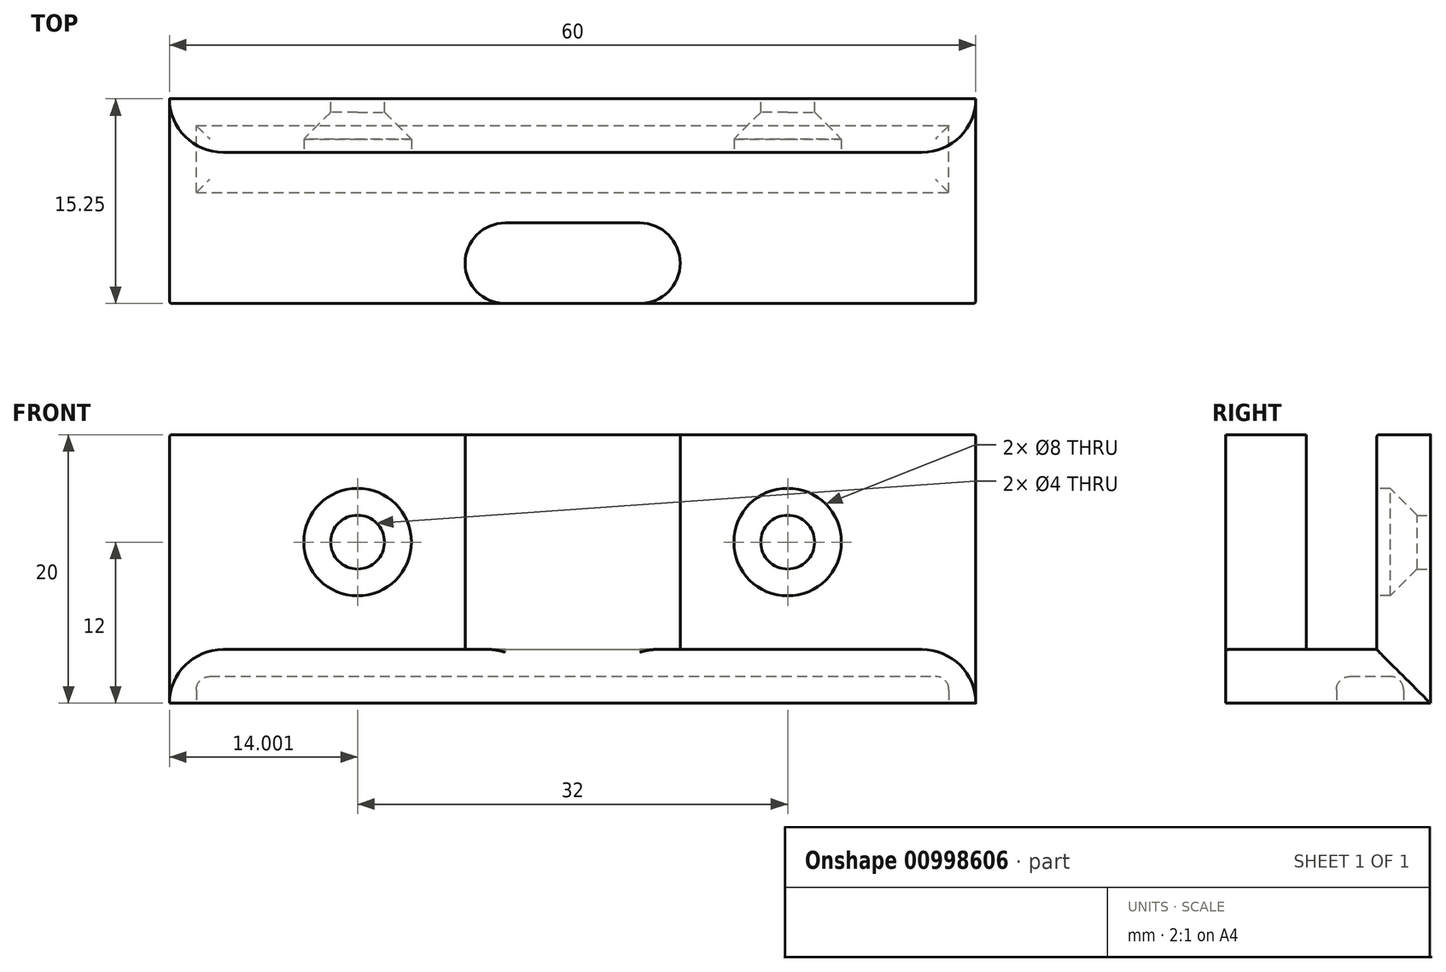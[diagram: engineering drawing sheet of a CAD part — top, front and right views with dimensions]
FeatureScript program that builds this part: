
annotation { "Feature Type Name" : "Feature", "Feature Type Description" : "" }
export const myFeature = defineFeature(function(context is Context, id is Id, definition is map)
    precondition{}
    {
        {
            var Q0;
            Q0=qCreatedBy(makeId("Top.planeOp"),FACE);
            var sketch = newSketch(context, id + "F0", { "sketchPlane" : qUnion([Q0])});
            skLineSegment(sketch, "E0.bottom", {"start": v(-19.65, 15.3) * mm, "end": v(40.35, 15.3) * mm});
            skLineSegment(sketch, "E0.top", {"start": v(-19.65, 0.05) * mm, "end": v(40.35, 0.05) * mm});
            skLineSegment(sketch, "E0.left", {"start": v(-19.65, 15.3) * mm, "end": v(-19.65, 0.05) * mm});
            skLineSegment(sketch, "E0.right", {"start": v(40.35, 15.3) * mm, "end": v(40.35, 0.05) * mm});
            skSolve(sketch);
        }
        {
            var Q0;
            Q0=makeQuery(id+"F0.imprint","IMPRINT",FACE,{"disambiguationData":[TD([[makeQuery(id+"F0.imprint","IMPRINT",EDGE,{"derivedFrom":sQuery(id+"F0.wireOp",EDGE,"E0.bottom")}),-1.0]])]});
            extrude(context, id + "F1", {"entities" : qUnion([Q0]), "depth" : 4 * mm, "offsetDistance" : 25 * mm});
        }
        {
            var Q0;
            Q0=makeQuery(id+"F1.opExtrude","CAP_FACE",FACE,{"disambiguationData":[OSD([sQuery(id+"F0.wireOp",EDGE,"E0.bottom"),sQuery(id+"F0.wireOp",EDGE,"E0.top"),sQuery(id+"F0.wireOp",EDGE,"E0.left"),sQuery(id+"F0.wireOp",EDGE,"E0.right")])],"isStart":false});
            var sketch = newSketch(context, id + "F2", { "sketchPlane" : qUnion([Q0])});
            skLineSegment(sketch, "E1.bottom", {"start": v(-19.65, 15.3) * mm, "end": v(40.35, 15.3) * mm});
            skLineSegment(sketch, "E1.top", {"start": v(-19.65, 11.3) * mm, "end": v(40.35, 11.3) * mm});
            skLineSegment(sketch, "E1.left", {"start": v(-19.65, 15.3) * mm, "end": v(-19.65, 11.3) * mm});
            skLineSegment(sketch, "E1.right", {"start": v(40.35, 15.3) * mm, "end": v(40.35, 11.3) * mm});
            skPoint(sketch, "E2", {"position": v(2.35, 3.05) * mm});
            skPoint(sketch, "E3", {"position": v(18.35, 3.05) * mm});
            skPoint(sketch, "E4", {"position": v(15.35, 6.05) * mm});
            skPoint(sketch, "E5", {"position": v(15.35, 0.05) * mm});
            skPoint(sketch, "E6", {"position": v(5.35, 6.05) * mm});
            skPoint(sketch, "E7", {"position": v(5.35, 0.05) * mm});
            skArc(sketch, "E8", {"start": v(5.35, 6.05) * mm, "mid": v(2.35, 3.05) * mm, "end": v(5.35, 0.05) * mm});
            skArc(sketch, "E9", {"start": v(15.35, 6.05) * mm, "mid": v(18.35, 3.05) * mm, "end": v(15.35, 0.05) * mm});
            skLineSegment(sketch, "E10", {"start": v(5.35, 6.05) * mm, "end": v(15.35, 6.05) * mm});
            skLineSegment(sketch, "E11", {"start": v(5.35, 0.05) * mm, "end": v(15.35, 0.05) * mm});
            skSolve(sketch);
        }
        {
            var Q0;
            Q0 = qSketchRegion(id + "F2", true);
            extrude(context, id + "F3", {"entities" : qUnion([Q0]), "operationType" : NewBodyOperationType.ADD, "depth" : 16 * mm, "offsetDistance" : 25 * mm});
        }
        {
            var Q0;
            Q0=makeQuery(id+"F3.opExtrude","SWEPT_FACE",FACE,{"disambiguationData":[OSD([sQuery(id+"F2.wireOp",EDGE,"E1.top")])]});
            var sketch = newSketch(context, id + "F4", { "sketchPlane" : qUnion([Q0])});
            skCircle(sketch, "E12", {"center": v(-5.65, 12) * mm, "radius": 4 * mm});
            skCircle(sketch, "E13", {"center": v(26.35, 12) * mm, "radius": 4 * mm});
            skSolve(sketch);
        }
        {
            var Q0;
            Q0 = qSketchRegion(id + "F4", true);
            extrude(context, id + "F5", {"entities" : qUnion([Q0]), "operationType" : NewBodyOperationType.REMOVE, "oppositeDirection" : true, "depth" : 1 * mm, "offsetDistance" : 25 * mm});
        }
        {
            var Q0;
            Q0=makeQuery(id+"F5.boolean.opBoolean","COPY",FACE,{"derivedFrom":makeQuery(id+"F5.opExtrude","CAP_FACE",FACE,{"disambiguationData":[OSD([sQuery(id+"F4.wireOp",EDGE,"E12")])],"isStart":false})});
            var Q1;
            Q1=makeQuery(id+"F5.boolean.opBoolean","COPY",FACE,{"derivedFrom":makeQuery(id+"F5.opExtrude","CAP_FACE",FACE,{"disambiguationData":[OSD([sQuery(id+"F4.wireOp",EDGE,"E13")])],"isStart":false})});
            extrude(context, id + "F6", {"entities" : qUnion([Q0, Q1]), "operationType" : NewBodyOperationType.REMOVE, "oppositeDirection" : true, "depth" : 25 * mm, "offsetDistance" : 25 * mm, "hasDraft" : true, "draftAngle" : 45 * degree, "draftPullDirection" : true});
        }
        {
            var Q0;
            Q0=makeQuery(id+"F3.boolean.opBoolean","MERGE",FACE,{"derivedFrom":[makeQuery(id+"F1.opExtrude","SWEPT_FACE",FACE,{"disambiguationData":[OSD([sQuery(id+"F0.wireOp",EDGE,"E0.bottom")])]}),makeQuery(id+"F3.opExtrude","SWEPT_FACE",FACE,{"disambiguationData":[OSD([sQuery(id+"F2.wireOp",EDGE,"E1.bottom")])]})]});
            var sketch = newSketch(context, id + "F7", { "sketchPlane" : qUnion([Q0])});
            skCircle(sketch, "E14", {"center": v(-26.35, 12) * mm, "radius": 2 * mm});
            skCircle(sketch, "E15", {"center": v(5.65, 12) * mm, "radius": 2 * mm});
            skSolve(sketch);
        }
        {
            var Q0;
            Q0 = qSketchRegion(id + "F7", true);
            extrude(context, id + "F8", {"entities" : qUnion([Q0]), "operationType" : NewBodyOperationType.REMOVE, "oppositeDirection" : true, "depth" : 25 * mm, "offsetDistance" : 25 * mm});
        }
        {
            var Q0;
            Q0=makeQuery(id+"F1.opExtrude","CAP_EDGE",EDGE,{"disambiguationData":[OSD([sQuery(id+"F0.wireOp",EDGE,"E0.left")])],"isStart":false});
            var Q1;
            Q1=makeQuery(id+"F3.opExtrude","SWEPT_EDGE",EDGE,{"disambiguationData":[OSD([sQuery(id+"F0.wireOp",EDGE,"E0.left"),sQuery(id+"F2.wireOp",EDGE,"E1.top"),sQuery(id+"F2.wireOp",EDGE,"E1.left")])]});
            var Q2;
            Q2=makeQuery(id+"F3.opExtrude","SWEPT_EDGE",EDGE,{"disambiguationData":[OSD([sQuery(id+"F0.wireOp",EDGE,"E0.right"),sQuery(id+"F2.wireOp",EDGE,"E1.top"),sQuery(id+"F2.wireOp",EDGE,"E1.right")])]});
            var Q3;
            Q3=makeQuery(id+"F1.opExtrude","CAP_EDGE",EDGE,{"disambiguationData":[OSD([sQuery(id+"F0.wireOp",EDGE,"E0.right")])],"isStart":false});
            fillet(context, id + "F9", {"entities" : qUnion([Q0, Q1, Q2, Q3]), "radius" : 4 * mm, "tangentPropagation" : true, "allowEdgeOverflow" : false});
        }
        {
            var Q0;
            Q0=makeQuery(id+"F3.opExtrude","CAP_EDGE",EDGE,{"disambiguationData":[OSD([sQuery(id+"F2.wireOp",EDGE,"E1.top")])],"isStart":true});
            var Q1;
            {var subQ0=sQuery(id+"F0.wireOp",EDGE,"E0.left");var subQ1=sQuery(id+"F0.wireOp",EDGE,"E0.top");Q1=makeQuery(id+"F3.boolean.opBoolean","SPLIT",EDGE,{"disambiguationData":[TD([makeQuery(id+"F1.opExtrude","SWEPT_FACE",FACE,{"disambiguationData":[OSD([subQ0])]})])],"derivedFrom":makeQuery(id+"F1.opExtrude","CAP_EDGE",EDGE,{"disambiguationData":[OSD([subQ1])],"isStart":false})});}
            var Q2;
            {var subQ0=sQuery(id+"F0.wireOp",EDGE,"E0.right");var subQ1=sQuery(id+"F0.wireOp",EDGE,"E0.top");Q2=makeQuery(id+"F3.boolean.opBoolean","SPLIT",EDGE,{"disambiguationData":[TD([makeQuery(id+"F1.opExtrude","SWEPT_FACE",FACE,{"disambiguationData":[OSD([subQ0])]})])],"derivedFrom":makeQuery(id+"F1.opExtrude","CAP_EDGE",EDGE,{"disambiguationData":[OSD([subQ1])],"isStart":false})});}
            var Q3;
            Q3=makeQuery(id+"F3.opExtrude","CAP_EDGE",EDGE,{"disambiguationData":[OSD([sQuery(id+"F2.wireOp",EDGE,"E1.top")])],"isStart":false});
            fillet(context, id + "F10", {"entities" : qUnion([Q0, Q1, Q2, Q3]), "radius" : 0.2 * mm, "tangentPropagation" : true, "allowEdgeOverflow" : false});
        }
        {
            var Q0;
            Q0=makeQuery(id+"F1.opExtrude","CAP_FACE",FACE,{"disambiguationData":[OSD([sQuery(id+"F0.wireOp",EDGE,"E0.bottom"),sQuery(id+"F0.wireOp",EDGE,"E0.top"),sQuery(id+"F0.wireOp",EDGE,"E0.left"),sQuery(id+"F0.wireOp",EDGE,"E0.right")])],"isStart":true});
            var sketch = newSketch(context, id + "F11", { "sketchPlane" : qUnion([Q0])});
            skLineSegment(sketch, "E16.bottom", {"start": v(-17.65, -8.3) * mm, "end": v(38.35, -8.3) * mm});
            skLineSegment(sketch, "E16.top", {"start": v(-17.65, -13.3) * mm, "end": v(38.35, -13.3) * mm});
            skLineSegment(sketch, "E16.left", {"start": v(-17.65, -8.3) * mm, "end": v(-17.65, -13.3) * mm});
            skLineSegment(sketch, "E16.right", {"start": v(38.35, -8.3) * mm, "end": v(38.35, -13.3) * mm});
            skSolve(sketch);
        }
        {
            var Q0;
            Q0 = qSketchRegion(id + "F11", true);
            extrude(context, id + "F12", {"entities" : qUnion([Q0]), "operationType" : NewBodyOperationType.REMOVE, "oppositeDirection" : true, "depth" : 2 * mm, "offsetDistance" : 25 * mm});
        }
        {
            var Q0;
            Q0=makeQuery(id+"F12.boolean.opBoolean","COPY",EDGE,{"derivedFrom":makeQuery(id+"F12.opExtrude","CAP_EDGE",EDGE,{"disambiguationData":[OSD([sQuery(id+"F11.wireOp",EDGE,"E16.bottom")])],"isStart":false})});
            var Q1;
            Q1=makeQuery(id+"F12.boolean.opBoolean","COPY",EDGE,{"derivedFrom":makeQuery(id+"F12.opExtrude","CAP_EDGE",EDGE,{"disambiguationData":[OSD([sQuery(id+"F11.wireOp",EDGE,"E16.left")])],"isStart":false})});
            var Q2;
            Q2=makeQuery(id+"F12.boolean.opBoolean","COPY",EDGE,{"derivedFrom":makeQuery(id+"F12.opExtrude","CAP_EDGE",EDGE,{"disambiguationData":[OSD([sQuery(id+"F11.wireOp",EDGE,"E16.top")])],"isStart":false})});
            var Q3;
            Q3=makeQuery(id+"F12.boolean.opBoolean","COPY",EDGE,{"derivedFrom":makeQuery(id+"F12.opExtrude","CAP_EDGE",EDGE,{"disambiguationData":[OSD([sQuery(id+"F11.wireOp",EDGE,"E16.right")])],"isStart":false})});
            fillet(context, id + "F13", {"entities" : qUnion([Q0, Q1, Q2, Q3]), "radius" : 1 * mm, "tangentPropagation" : true, "allowEdgeOverflow" : false});
        }
    });
